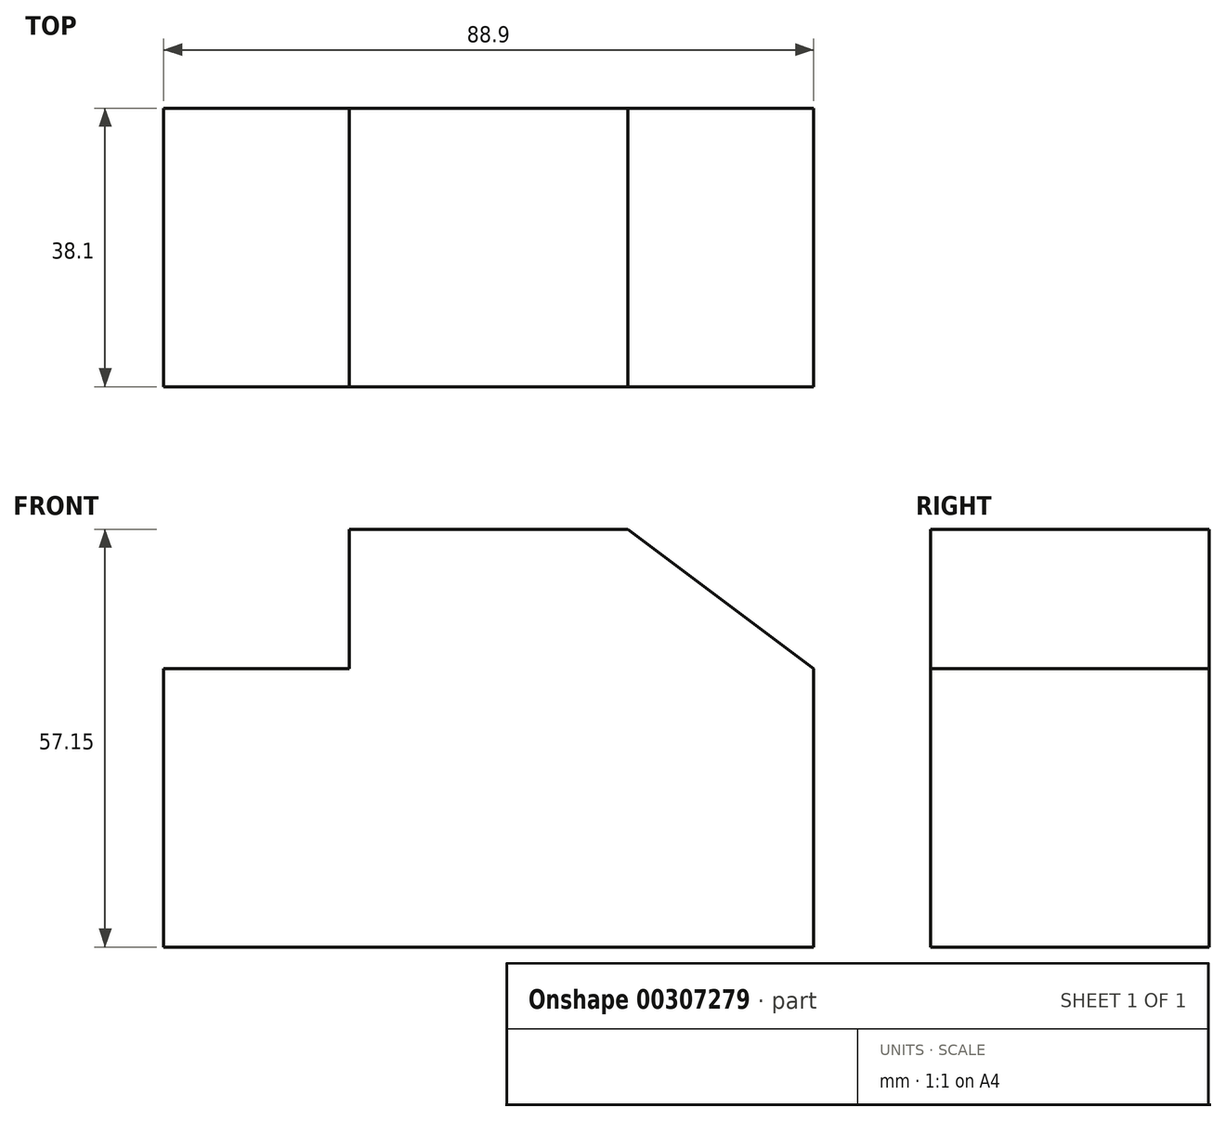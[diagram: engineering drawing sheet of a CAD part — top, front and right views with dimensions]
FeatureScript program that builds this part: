
annotation { "Feature Type Name" : "Feature", "Feature Type Description" : "" }
export const myFeature = defineFeature(function(context is Context, id is Id, definition is map)
    precondition{}
    {
        {
            var Q0;
            Q0=qCreatedBy(makeId("Front.planeOp"),FACE);
            var sketch = newSketch(context, id + "F0", { "sketchPlane" : qUnion([Q0])});
            skLineSegment(sketch, "E0", {"start": v(-30.85, -36.49) * mm, "end": v(45.35, -36.49) * mm});
            skLineSegment(sketch, "E1", {"start": v(45.35, -36.49) * mm, "end": v(45.35, 1.61) * mm});
            skLineSegment(sketch, "E2", {"start": v(45.35, 1.61) * mm, "end": v(19.95, 20.66) * mm});
            skLineSegment(sketch, "E3", {"start": v(19.95, 20.66) * mm, "end": v(-18.15, 20.66) * mm});
            skLineSegment(sketch, "E4", {"start": v(-18.15, 20.66) * mm, "end": v(-18.15, 1.61) * mm});
            skLineSegment(sketch, "E5", {"start": v(-18.15, 1.61) * mm, "end": v(-43.55, 1.61) * mm});
            skLineSegment(sketch, "E6", {"start": v(-43.55, 1.61) * mm, "end": v(-43.55, -36.49) * mm});
            skLineSegment(sketch, "E7", {"start": v(-43.55, -36.49) * mm, "end": v(-30.85, -36.49) * mm});
            skSolve(sketch);
        }
        {
            var Q0;
            Q0=makeQuery(id+"F0.imprint","IMPRINT",FACE,{"disambiguationData":[TD([[makeQuery(id+"F0.imprint","IMPRINT",EDGE,{"derivedFrom":sQuery(id+"F0.wireOp",EDGE,"E0")}),1.0]])]});
            extrude(context, id + "F1", {"entities" : qUnion([Q0]), "depth" : 38.1 * mm});
        }
    });
